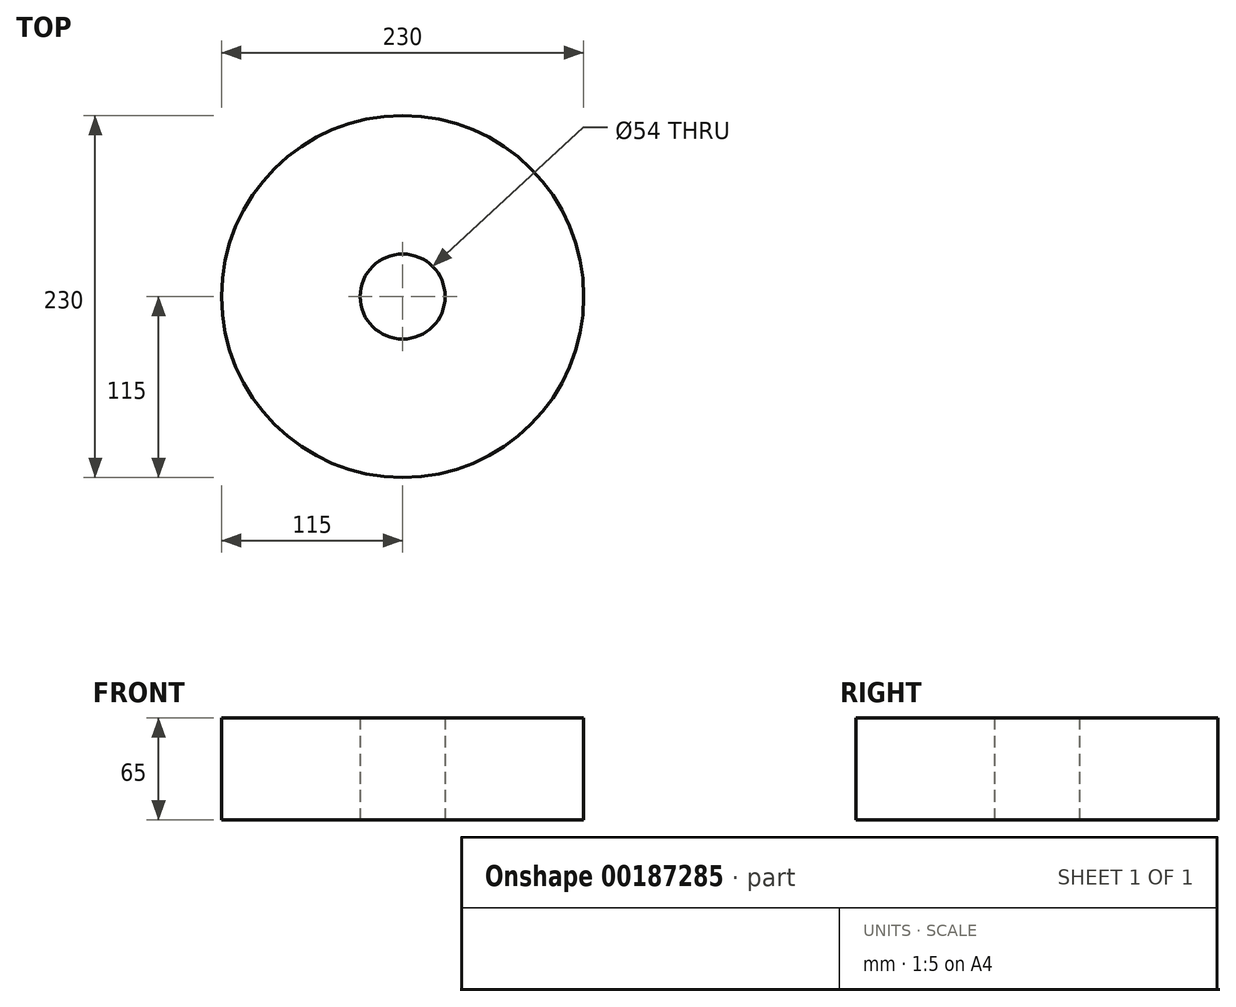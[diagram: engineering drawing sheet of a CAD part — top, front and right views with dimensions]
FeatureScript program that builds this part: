
annotation { "Feature Type Name" : "Feature", "Feature Type Description" : "" }
export const myFeature = defineFeature(function(context is Context, id is Id, definition is map)
    precondition{}
    {
        {
            var Q0;
            Q0=qCreatedBy(makeId("Top.planeOp"),FACE);
            var sketch = newSketch(context, id + "F0", { "sketchPlane" : qUnion([Q0])});
            skCircle(sketch, "E0", {"center": v(0, 0) * mm, "radius": 115 * mm});
            skCircle(sketch, "E1", {"center": v(0, 0) * mm, "radius": 27 * mm});
            skSolve(sketch);
        }
        {
            var Q0;
            Q0=makeQuery(id+"F0.imprint","IMPRINT",FACE,{"disambiguationData":[TD([[makeQuery(id+"F0.imprint","IMPRINT",EDGE,{"derivedFrom":sQuery(id+"F0.wireOp",EDGE,"E0")}),1.0]])]});
            extrude(context, id + "F1", {"entities" : qUnion([Q0]), "offsetDistance" : 25 * mm, "depth" : 65 * mm});
        }
    });
